# Revit family: RN 55049 Optipress-Therm-Flanschübergang PN 16
name_source: partatom
category: Rohrformteile
units: mm (PartAtom-declared; Revit-internal decimal feet)

## family parameters
Arbeitsebenenbasiert = Nein
Beim Laden mit Abzugskörper schneiden = Nein
Bemaßung runder Anschluss = Durchmesser verwenden
Gemeinsam genutzt = Nein
Immer vertikal = Ja
OmniClass-Nummer = 23.60.30.11.14
OmniClass-Titel = Pipework Fittings
Teiletyp = Flansch

## types (1)
- Var
    Bauelement = 03.02.01.02
    Beschreibung = Flanschübergang
    Hersteller = R. Nussbaum AG
    IfcDescription = Flanschübergang
    IfcExportAs = IfcPipeFitting
    IfcExportType = USERDEFINED
    Modell = 55049.71
    RN_LOD = LOD 400
    RN_Manufactur = R. Nussbaum AG
    RN_Mat = Stahl 1.0308
    RN_Serie = Optipress therm
    RN_tab = RN_55049
    Typenkommentare = Optipress-Therm-Flanschübergang PN 16 Var
    URL = http://www.nussbaum.ch
    type_index = 1

## geometry (parser evidence)
native form markers: Sweep x5
no freeform markers — native parametric forms only
